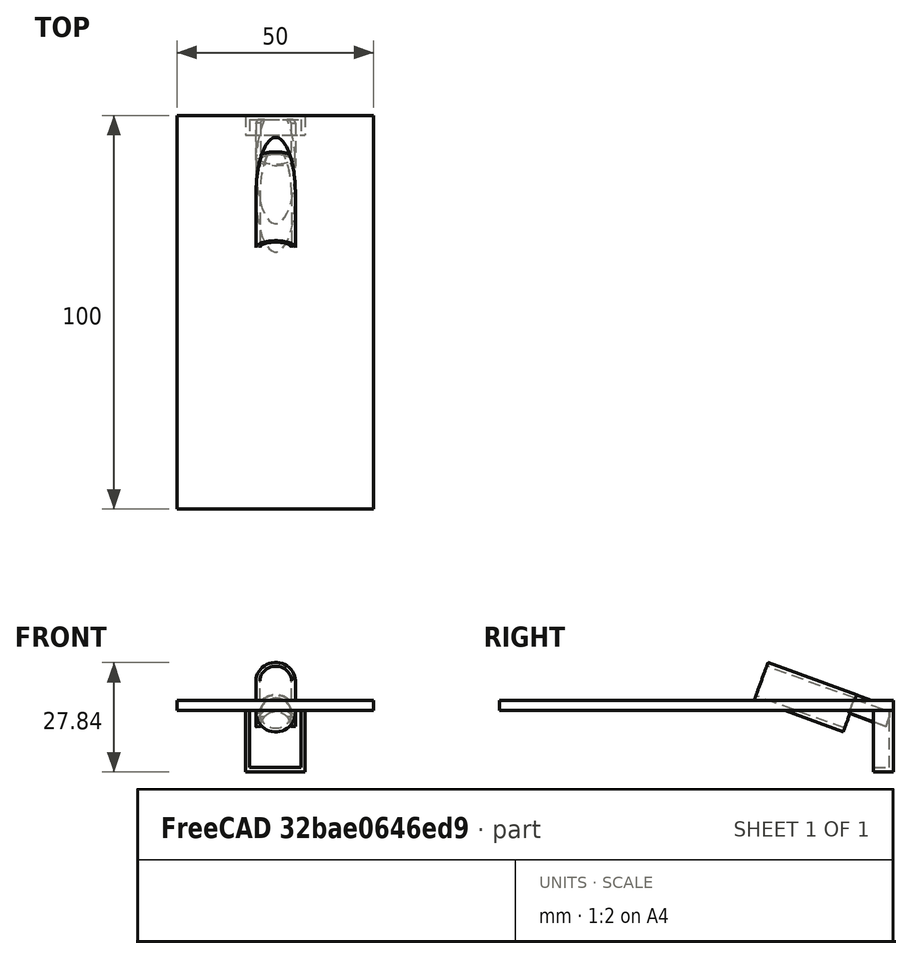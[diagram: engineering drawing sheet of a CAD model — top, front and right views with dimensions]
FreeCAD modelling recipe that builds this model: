
FCSTD DOCUMENT  (FreeCAD 0.21R33694 (Git))
Label: reward_chute_Wall_v4
License: All rights reserved
LicenseURL: https://en.wikipedia.org/wiki/All_rights_reserved
objects: Part::Box×3, Part::Cut×2, Sketcher::SketchObject×1, Part::Extrusion×1, Part::Cylinder×1, Part::FeaturePython×1, Part::MultiFuse×1
note: 10 computed .brp shape members not serialized (recipe doc carries the construction recipe); baked Part::Feature solids carry a one-line shape summary decoded from their .brp

FEATURE [Part::Box] Box  label="Cube"
  AttacherType = Attacher::AttachEngine3D
  Height = 2.6
  Length = 50
  Width = 100
FEATURE [Sketcher::SketchObject] Sketch
  FullyConstrained = false
  sketch-geometry (4):
    g0: ArcOfCircle CenterX=25.1024 CenterY=25.146 CenterZ=0 NormalX=0 NormalY=0 NormalZ=1 AngleXU=0 Radius=3.90266 StartAngle=0 EndAngle=3.14159
    g1: ArcOfCircle CenterX=25.1024 CenterY=25.146 CenterZ=0 NormalX=0 NormalY=0 NormalZ=1 AngleXU=0 Radius=5.0073 StartAngle=0 EndAngle=3.1459
    g2: LineSegment StartX=29.005 StartY=25.146 StartZ=0 EndX=30.1097 EndY=25.146 EndZ=0
    g3: LineSegment StartX=21.1997 StartY=25.146 StartZ=0 EndX=20.0951 EndY=25.1244 EndZ=0
  constraints (6):
    c: Coincident(g1,g0)
    c: Coincident(g2,g0)
    c: Coincident(g2,g1)
    c: Horizontal(g2)
    c: Coincident(g3,g0)
    c: Coincident(g3,g1)
FEATURE [Part::Extrusion] Extrude
  Base = -> Sketch
  Dir = (0,0,1)
  DirMode = 2
  FaceMakerClass = Part::FaceMakerBullseye
  LengthFwd = 10
  LengthRev = 0
  Placement = pos=(0,89.5,-27.7) rot=(1,0,0;1.22173rad)
  Solid = true
  Symmetric = false
FEATURE [Part::Cylinder] Cylinder
  Angle = 360
  AttacherType = Attacher::AttachEngine3D
  FirstAngle = 0
  Height = 35
  Placement = pos=(25.1,98,-4) rot=(1,0,0;1.22173rad)
  Radius = 4
  SecondAngle = 0
FEATURE [Part::FeaturePython] Tube  # WARN: FeaturePython — macro-defined, semantics opaque (R4)
  AttacherType = Attacher::AttachEngine3D
  Height = 24
  InnerRadius = 4
  OuterRadius = 5
  Placement = pos=(25.1,89,-0.7) rot=(1,0,0;1.22173rad)
FEATURE [Part::Box] Box001  label="Cube001"
  AttacherType = Attacher::AttachEngine3D
  Height = 18
  Length = 15
  Placement = pos=(17.5,45,-7.13) rot=(0,0,1;0rad)
  Width = 5
FEATURE [Part::Box] Box002  label="Cube002"
  AttacherType = Attacher::AttachEngine3D
  Height = 16
  Length = 13
  Placement = pos=(18.5,45,-6) rot=(0,0,1;0rad)
  Width = 4
FEATURE [Part::Cut] Cut001
  Base = -> Box001
  Placement = pos=(0,50,-8.5) rot=(0,0,1;0rad)
  Tool = -> Box002
FEATURE [Part::Cut] Cut
  Base = -> Box
  Tool = -> Cylinder
FEATURE [Part::MultiFuse] Fusion
  Shapes = -> [Extrude,Tube,Cut001,Cut]
